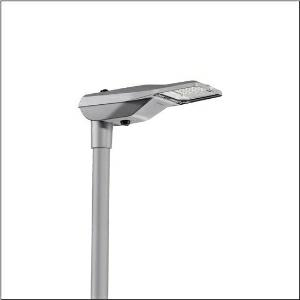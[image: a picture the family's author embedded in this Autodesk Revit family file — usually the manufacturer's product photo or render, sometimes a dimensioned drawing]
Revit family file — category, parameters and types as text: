
# Revit family: streetlight_sl_21_iq_micro___st1_0a_5xe1d61y08cb_da7e
name_source: partatom
category: Lighting Fixtures
units: mm (PartAtom-declared; Revit-internal decimal feet)

## family parameters
Cut with Voids When Loaded = No
Host = Face
Light Source = No
Part Type = Normal
Room Calculation Point = No
Round Connector Dimension = Use Diameter
Shared = No

## types (1)
- --- (1 x LED, 2500 lm, 19.1 W, 2700K)
    Apparent Load = 19 VA
    CIE Flux Codes = 37 72 97 100 100
    Color Rendering = 70
    Color Temperature = 2700K
    Default Elevation = 1800 mm
    Description = Streetlight SL 21 iQ micro, mast luminaire, primary light control with lens, of PMMA, primary optical cover: cover, of toughened safety glass, transparent, light distribution: ST1.0a, light emission: direct distribution, primary light characteristic: asymmetric, installation type: post-top, side-entry, LED, High Power LED, rated luminous flux: 2.500lm, luminous efficacy: 131lm/W, light colour: 727, colour temperature: 2700K, control gear: iQ-Street Remote, D4i with power reduction, control: pre-setting: logarithmic dimming characteristic, Street-Remote, Auto-Match, Temp-Guard, Lumen-Switch, Night-Set, Smart-Wire, Light-Fading, Desk-Remote (wireless, voltage-free reading and setting of iQ features in the workshop via application-optimized NFC function/RFID function), optimised constant luminous flux control (CLO 2.0), mains connection: 220..240V, AC, 50/60Hz, start of lifetime: 19W, end of service life: 20W, reduction: 9W, luminaire housing, of diecast aluminium, powder-coated, SITECO metallic grey (DB 702S), corrosivity category C5 high according to DIN EN ISO 12944, please order mast flange separately, inclination adjustable: 0°, 5°, 10°, 15°, sealing non-destructively replaceable, multi-level sealing system, length: 528mm, width: 235mm, height: 110mm, mast flange for spigot size: 42mm (side-entry): 5XC10008XM4, 60/48mm (side-entry/post-top): 5XC10108XM2, 76/60mm (side-entry/post-top): 5XC10108XM1, mounting height: 4..8m, Smart Interface below and above, protection rating (complete): IP66, insulation class (complete): insulation class II (safety insulation), certification: CE, ENEC, ENEC+, VDE, impact resistance: IK10, permissible operating ambient temperature for outdoor applications: -40..+50°C, standard-compliant lighting for roads and squares, packaging unit: 1 piece

Light Distribution: ST1.0a
    Height = 110 mm
    Lamp = 1 x LED
    Lamp Light Flux = 2500 lm
    Lamp Power = 19.1 W
    Lamp count = 1
    Length = 528 mm
    Luminous efficacy = 131 lm/W
    Manufacturer = Siteco
    ModVariant = No
    Model = 5XE1D61Y08CB
    Number of Poles = 1
    OnlyDefault = Yes
    Power Factor = 1
    Product Name = Streetlight SL 21 iQ micro | ST1.0a
    Product group = mast luminaire | pylon top
    ProductGroupID = 6100
    Protection Class = Protection class II
    Protection Degree = IP 66
    RLX_Detail_Level = 1
    RLX_Emergency_Light_Flux = 0 lm
    RLX_Emergency_Type = 0
    RLX_Emergency_Type_DB = No
    RlxData = <blob elided: 98605 chars, md5=3bed31ff>
    Socket = socket
    Standby Power = 0 W
    System Light Flux = 2500 lm
    System Power = 19 W
    Type Comments = factory setting: luminous flux: 100 % | dim-lin: 254 | 387 mA
    Type Image = l_1007239.jpg
    URL = http://relux.com
    VarID = @adj_115655
    Voltage = 0 V
    Weight = 0.00 kg
    Width = 235 mm

## geometry (parser evidence)
native form markers: Blend x4, Sweep x10
no freeform markers — native parametric forms only
